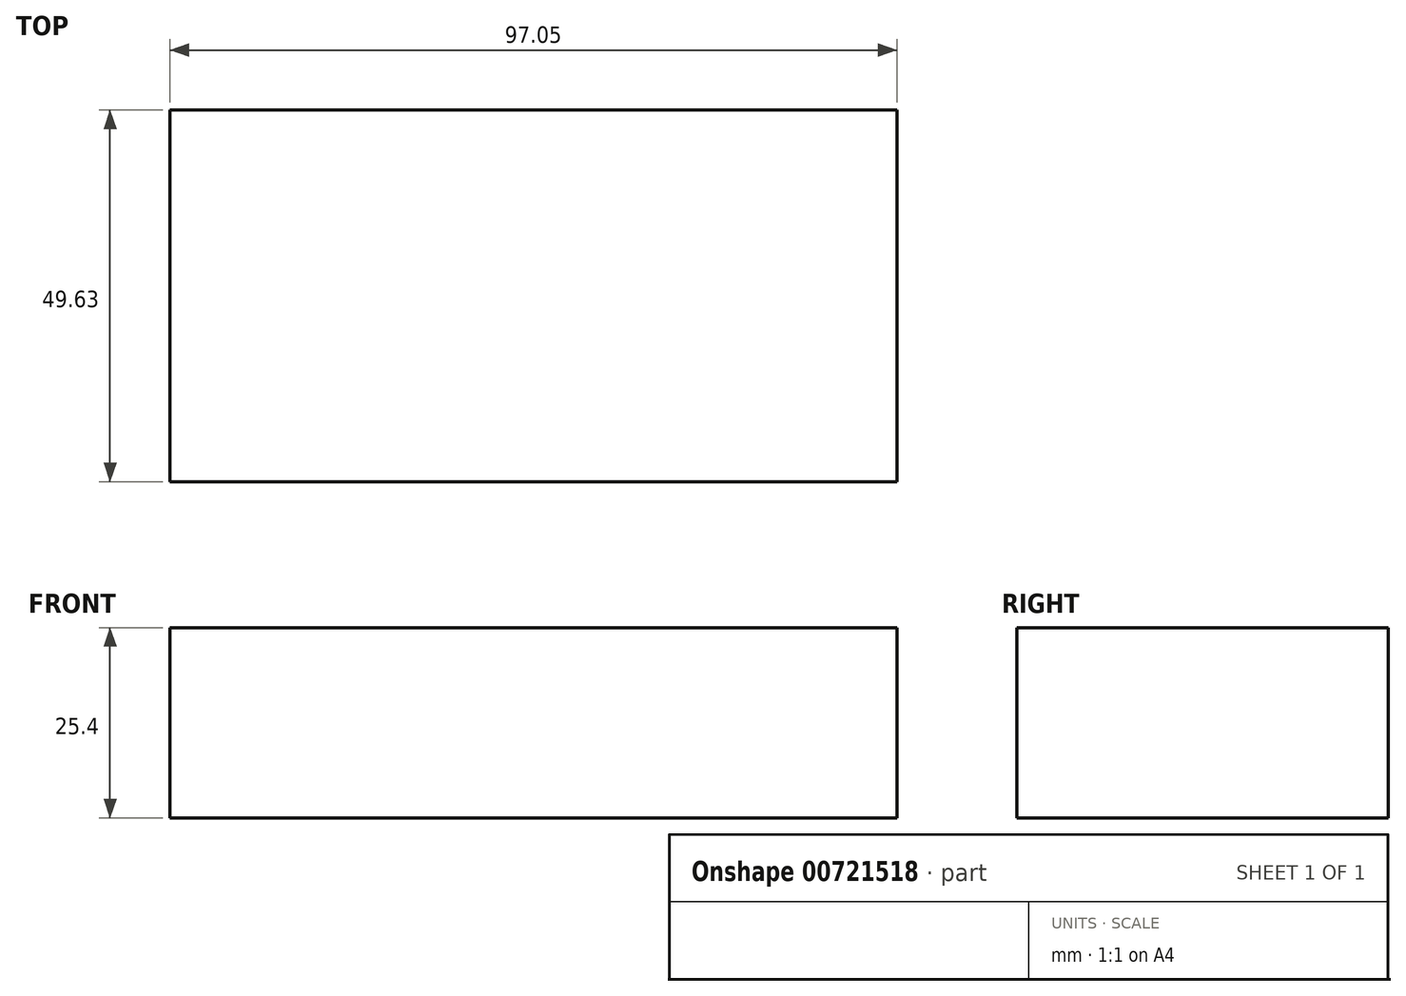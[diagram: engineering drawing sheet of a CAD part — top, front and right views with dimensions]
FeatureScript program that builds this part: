
annotation { "Feature Type Name" : "Feature", "Feature Type Description" : "" }
export const myFeature = defineFeature(function(context is Context, id is Id, definition is map)
    precondition{}
    {
        {
            var Q0;
            Q0=qCreatedBy(makeId("Top.planeOp"),FACE);
            var sketch = newSketch(context, id + "F0", { "sketchPlane" : qUnion([Q0])});
            skLineSegment(sketch, "E0.bottom", {"start": v(-50.1, -26.02) * mm, "end": v(46.95, -26.02) * mm});
            skLineSegment(sketch, "E0.top", {"start": v(-50.1, 23.61) * mm, "end": v(46.95, 23.61) * mm});
            skLineSegment(sketch, "E0.left", {"start": v(-50.1, -26.02) * mm, "end": v(-50.1, 23.61) * mm});
            skLineSegment(sketch, "E0.right", {"start": v(46.95, -26.02) * mm, "end": v(46.95, 23.61) * mm});
            skSolve(sketch);
        }
        {
            var Q0;
            Q0 = qSketchRegion(id + "F0", true);
            extrude(context, id + "F1", {"entities" : qUnion([Q0]), "depth" : 25.4 * mm, "offsetDistance" : 25.4 * mm});
        }
    });
